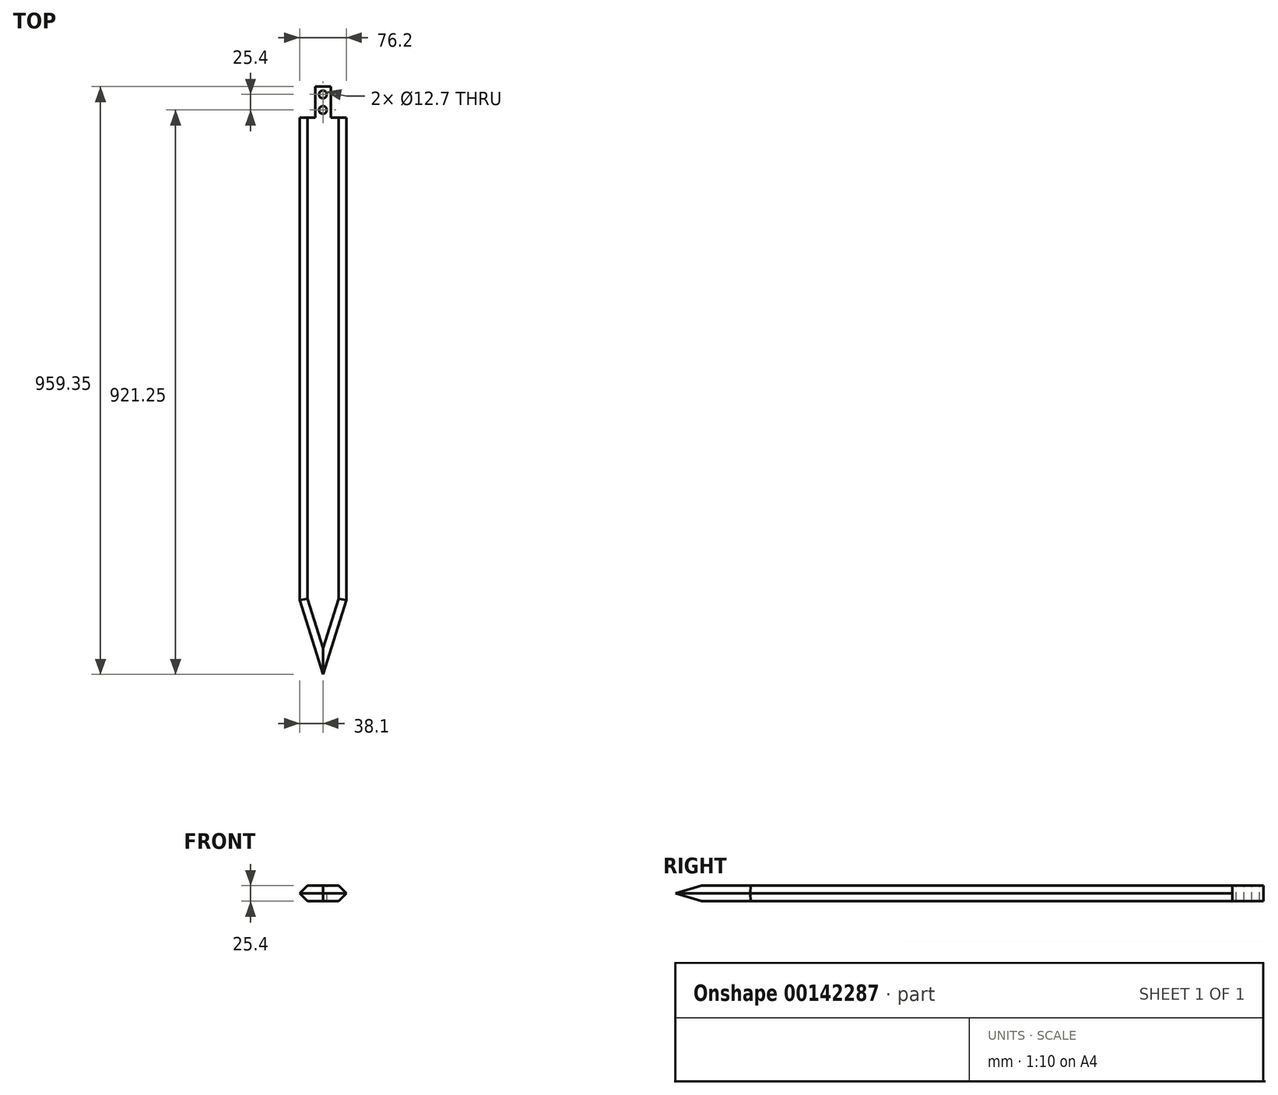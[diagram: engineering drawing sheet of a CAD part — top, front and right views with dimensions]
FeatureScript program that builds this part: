
annotation { "Feature Type Name" : "Feature", "Feature Type Description" : "" }
export const myFeature = defineFeature(function(context is Context, id is Id, definition is map)
    precondition{}
    {
        {
            var Q0;
            Q0=qCreatedBy(makeId("Top.planeOp"),FACE);
            var sketch = newSketch(context, id + "F0", { "sketchPlane" : qUnion([Q0])});
            skLineSegment(sketch, "E0", {"start": v(-38.1, -29.35) * mm, "end": v(38.1, -29.35) * mm});
            skLineSegment(sketch, "E1", {"start": v(-38.1, -29.35) * mm, "end": v(-38.1, -816.75) * mm});
            skLineSegment(sketch, "E2", {"start": v(-38.1, -816.75) * mm, "end": v(0, -937.9) * mm});
            skLineSegment(sketch, "E3", {"start": v(0, -937.9) * mm, "end": v(38.1, -816.75) * mm});
            skLineSegment(sketch, "E4", {"start": v(38.1, -816.75) * mm, "end": v(38.1, -29.35) * mm});
            skLineSegment(sketch, "E5", {"start": v(-12.7, -29.35) * mm, "end": v(-12.7, 21.45) * mm});
            skLineSegment(sketch, "E6", {"start": v(-12.7, 21.45) * mm, "end": v(12.7, 21.45) * mm});
            skLineSegment(sketch, "E7", {"start": v(12.7, 21.45) * mm, "end": v(12.7, -29.35) * mm});
            skPoint(sketch, "E8.orphan", {"position": v(0, -29.35) * mm});
            skSolve(sketch);
        }
        {
            var Q0;
            {var subQ0=sQuery(id+"F0.wireOp",EDGE,"E1");Q0=makeQuery(id+"F0.imprint","IMPRINT",FACE,{"disambiguationData":[TD([[makeQuery(id+"F0.imprint","IMPRINT",EDGE,{"derivedFrom":subQ0}),1.0]])]});}
            var Q1;
            {var subQ0=sQuery(id+"F0.wireOp",EDGE,"E5");Q1=makeQuery(id+"F0.imprint","IMPRINT",FACE,{"disambiguationData":[TD([[makeQuery(id+"F0.imprint","IMPRINT",EDGE,{"derivedFrom":subQ0}),-1.0]])]});}
            extrude(context, id + "F1", {"entities" : qUnion([Q0, Q1]), "endBound" : BoundingType.SYMMETRIC, "depth" : 25.4 * mm});
        }
        {
            var Q0;
            Q0=makeQuery(id+"F1.opExtrude","CAP_EDGE",EDGE,{"disambiguationData":[OSD([sQuery(id+"F0.wireOp",EDGE,"E4")])],"isStart":false});
            var Q1;
            Q1=makeQuery(id+"F1.opExtrude","CAP_EDGE",EDGE,{"disambiguationData":[OSD([sQuery(id+"F0.wireOp",EDGE,"E3")])],"isStart":false});
            var Q2;
            Q2=makeQuery(id+"F1.opExtrude","CAP_EDGE",EDGE,{"disambiguationData":[OSD([sQuery(id+"F0.wireOp",EDGE,"E2")])],"isStart":false});
            var Q3;
            Q3=makeQuery(id+"F1.opExtrude","CAP_EDGE",EDGE,{"disambiguationData":[OSD([sQuery(id+"F0.wireOp",EDGE,"E1")])],"isStart":false});
            var Q4;
            Q4=makeQuery(id+"F1.opExtrude","CAP_EDGE",EDGE,{"disambiguationData":[OSD([sQuery(id+"F0.wireOp",EDGE,"E3")])],"isStart":true});
            var Q5;
            Q5=makeQuery(id+"F1.opExtrude","CAP_EDGE",EDGE,{"disambiguationData":[OSD([sQuery(id+"F0.wireOp",EDGE,"E1")])],"isStart":true});
            var Q6;
            Q6=makeQuery(id+"F1.opExtrude","CAP_EDGE",EDGE,{"disambiguationData":[OSD([sQuery(id+"F0.wireOp",EDGE,"E2")])],"isStart":true});
            var Q7;
            Q7=makeQuery(id+"F1.opExtrude","CAP_EDGE",EDGE,{"disambiguationData":[OSD([sQuery(id+"F0.wireOp",EDGE,"E4")])],"isStart":true});
            chamfer(context, id + "F2", {"entities" : qUnion([Q0, Q1, Q2, Q3, Q4, Q5, Q6, Q7]), "width" : 12.7 * mm, "tangentPropagation" : true});
        }
        {
            var Q0;
            Q0=makeQuery(id+"F1.opExtrude","CAP_FACE",FACE,{"disambiguationData":[OSD([sQuery(id+"F0.wireOp",EDGE,"E0"),sQuery(id+"F0.wireOp",EDGE,"E1"),sQuery(id+"F0.wireOp",EDGE,"E2"),sQuery(id+"F0.wireOp",EDGE,"E3"),sQuery(id+"F0.wireOp",EDGE,"E4"),sQuery(id+"F0.wireOp",EDGE,"E5"),sQuery(id+"F0.wireOp",EDGE,"E6"),sQuery(id+"F0.wireOp",EDGE,"E7")])],"isStart":false});
            var sketch = newSketch(context, id + "F3", { "sketchPlane" : qUnion([Q0])});
            skCircle(sketch, "E9", {"center": v(0, 8.75) * mm, "radius": 6.35 * mm});
            skCircle(sketch, "E10", {"center": v(0, -16.65) * mm, "radius": 6.35 * mm});
            skSolve(sketch);
        }
        {
            var Q0;
            Q0=makeQuery(id+"F3.imprint","IMPRINT",FACE,{"disambiguationData":[TD([[makeQuery(id+"F3.imprint","IMPRINT",EDGE,{"derivedFrom":sQuery(id+"F3.wireOp",EDGE,"E9")}),1.0]])]});
            var Q1;
            Q1=makeQuery(id+"F3.imprint","IMPRINT",FACE,{"disambiguationData":[TD([[makeQuery(id+"F3.imprint","IMPRINT",EDGE,{"derivedFrom":sQuery(id+"F3.wireOp",EDGE,"E10")}),1.0]])]});
            extrude(context, id + "F4", {"entities" : qUnion([Q0, Q1]), "operationType" : NewBodyOperationType.REMOVE, "endBound" : BoundingType.THROUGH_ALL, "oppositeDirection" : true, "depth" : 25.4 * mm});
        }
    });
